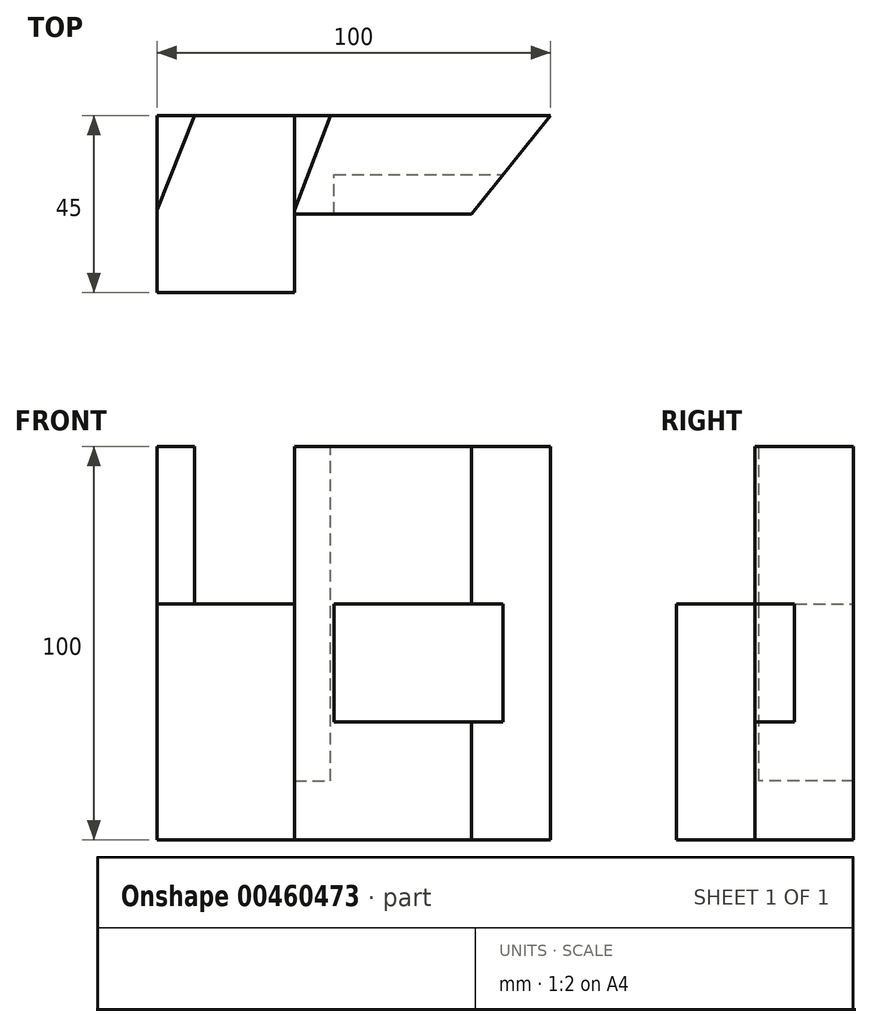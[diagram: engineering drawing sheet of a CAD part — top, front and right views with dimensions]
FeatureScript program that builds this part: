
annotation { "Feature Type Name" : "Feature", "Feature Type Description" : "" }
export const myFeature = defineFeature(function(context is Context, id is Id, definition is map)
    precondition{}
    {
        {
            var Q0;
            Q0=qCreatedBy(makeId("Top.planeOp"),FACE);
            var sketch = newSketch(context, id + "F0", { "sketchPlane" : qUnion([Q0])});
            skLineSegment(sketch, "E0.bottom", {"start": v(0, 0) * mm, "end": v(35, 0) * mm});
            skLineSegment(sketch, "E0.top", {"start": v(0, 45) * mm, "end": v(35, 45) * mm});
            skLineSegment(sketch, "E0.left", {"start": v(0, 0) * mm, "end": v(0, 45) * mm});
            skLineSegment(sketch, "E0.right", {"start": v(35, 0) * mm, "end": v(35, 45) * mm});
            skLineSegment(sketch, "E1.bottom", {"start": v(35, 45) * mm, "end": v(100, 45) * mm});
            skLineSegment(sketch, "E1.top", {"start": v(35, 20) * mm, "end": v(100, 20) * mm});
            skLineSegment(sketch, "E1.left", {"start": v(35, 45) * mm, "end": v(35, 20) * mm});
            skLineSegment(sketch, "E1.right", {"start": v(100, 45) * mm, "end": v(100, 20) * mm});
            skSolve(sketch);
        }
        {
            var Q0;
            Q0 = qSketchRegion(id + "F0", true);
            extrude(context, id + "F1", {"entities" : qUnion([Q0]), "depth" : 100 * mm});
        }
        {
            var Q0;
            Q0=makeQuery(id+"F1.opExtrude","CAP_FACE",FACE,{"disambiguationData":[OSD([sQuery(id+"F0.wireOp",EDGE,"E0.bottom"),sQuery(id+"F0.wireOp",EDGE,"E0.top"),sQuery(id+"F0.wireOp",EDGE,"E0.left"),sQuery(id+"F0.wireOp",EDGE,"E0.right"),sQuery(id+"F0.wireOp",EDGE,"E1.bottom"),sQuery(id+"F0.wireOp",EDGE,"E1.top"),sQuery(id+"F0.wireOp",EDGE,"E1.right")])],"isStart":false});
            var sketch = newSketch(context, id + "F2", { "sketchPlane" : qUnion([Q0])});
            skLineSegment(sketch, "E2", {"start": v(35, 20) * mm, "end": v(35, 21) * mm});
            skLineSegment(sketch, "E3", {"start": v(35, 21) * mm, "end": v(44.12, 45) * mm});
            skLineSegment(sketch, "E4", {"start": v(44.12, 45) * mm, "end": v(35, 45) * mm});
            skLineSegment(sketch, "E5", {"start": v(35, 45) * mm, "end": v(35, 21) * mm});
            skLineSegment(sketch, "E6", {"start": v(0, 45) * mm, "end": v(0, 21) * mm});
            skPoint(sketch, "E6.endSnap0", {"position": v(0, 22.5) * mm});
            skLineSegment(sketch, "E7", {"start": v(0, 21) * mm, "end": v(9.62, 45) * mm});
            skLineSegment(sketch, "E8", {"start": v(9.62, 45) * mm, "end": v(0, 45) * mm});
            skSolve(sketch);
        }
        {
            var Q0;
            Q0=makeQuery(id+"F1.opExtrude","CAP_FACE",FACE,{"disambiguationData":[OSD([sQuery(id+"F0.wireOp",EDGE,"E0.bottom"),sQuery(id+"F0.wireOp",EDGE,"E0.top"),sQuery(id+"F0.wireOp",EDGE,"E0.left"),sQuery(id+"F0.wireOp",EDGE,"E0.right"),sQuery(id+"F0.wireOp",EDGE,"E1.bottom"),sQuery(id+"F0.wireOp",EDGE,"E1.top"),sQuery(id+"F0.wireOp",EDGE,"E1.right")])],"isStart":true});
            cPlane(context, id + "F3", {"entities" : qUnion([Q0]), "cplaneType" : CPlaneType.OFFSET, "offset" : 60 * mm, "oppositeDirection" : true, "width" : 150 * mm, "height" : 150 * mm});
        }
        {
            var Q0;
            Q0=makeQuery(id+"F2.imprint","IMPRINT",FACE,{"disambiguationData":[TD([[makeQuery(id+"F2.imprint","IMPRINT",EDGE,{"derivedFrom":sQuery(id+"F2.wireOp",EDGE,"E2")}),1.0]])]});
            var Q1;
            Q1=qCreatedBy(id+"F3.planeOp",FACE);
            extrude(context, id + "F4", {"entities" : qUnion([Q0]), "operationType" : NewBodyOperationType.REMOVE, "endBound" : BoundingType.UP_TO_SURFACE, "oppositeDirection" : true, "endBoundEntityFace" : qUnion([Q1]), "depth" : 60 * mm});
        }
        {
            var Q0;
            Q0=makeQuery(id+"F2.imprint","IMPRINT",FACE,{"disambiguationData":[TD([[makeQuery(id+"F2.imprint","IMPRINT",EDGE,{"derivedFrom":sQuery(id+"F2.wireOp",EDGE,"E3")}),1.0]])]});
            extrude(context, id + "F5", {"entities" : qUnion([Q0]), "operationType" : NewBodyOperationType.REMOVE, "oppositeDirection" : true, "depth" : 85 * mm});
        }
        {
            var Q0;
            Q0=makeQuery(id+"F1.opExtrude","SWEPT_FACE",FACE,{"disambiguationData":[OSD([sQuery(id+"F0.wireOp",EDGE,"E1.right")])]});
            var sketch = newSketch(context, id + "F6", { "sketchPlane" : qUnion([Q0])});
            skLineSegment(sketch, "E9", {"start": v(20, 60) * mm, "end": v(20, 30) * mm});
            skLineSegment(sketch, "E10", {"start": v(20, 30) * mm, "end": v(30, 30) * mm});
            skLineSegment(sketch, "E11", {"start": v(30, 30) * mm, "end": v(30, 60) * mm});
            skLineSegment(sketch, "E12", {"start": v(30, 60) * mm, "end": v(20, 60) * mm});
            skSolve(sketch);
        }
        {
            var Q0;
            Q0 = qSketchRegion(id + "F6", true);
            extrude(context, id + "F7", {"entities" : qUnion([Q0]), "operationType" : NewBodyOperationType.REMOVE, "oppositeDirection" : true, "depth" : 55 * mm});
        }
        {
            var Q0;
            {var subQ0=sQuery(id+"F0.wireOp",EDGE,"E1.bottom");var subQ1=sQuery(id+"F0.wireOp",EDGE,"E0.top");var subQ2=sQuery(id+"F0.wireOp",EDGE,"E1.top");var subQ3=sQuery(id+"F0.wireOp",EDGE,"E1.right");var subQ4=sQuery(id+"F0.wireOp",EDGE,"E0.right");Q0=makeQuery(id+"F4.boolean.opBoolean","SPLIT",FACE,{"disambiguationData":[TD([makeQuery(id+"F1.opExtrude","SWEPT_FACE",FACE,{"disambiguationData":[OSD([subQ2])]})])],"derivedFrom":makeQuery(id+"F1.opExtrude","CAP_FACE",FACE,{"disambiguationData":[OSD([sQuery(id+"F0.wireOp",EDGE,"E0.bottom"),subQ1,sQuery(id+"F0.wireOp",EDGE,"E0.left"),subQ4,subQ0,subQ2,subQ3])],"isStart":false})});}
            var sketch = newSketch(context, id + "F8", { "sketchPlane" : qUnion([Q0])});
            skLineSegment(sketch, "E13", {"start": v(100, 45) * mm, "end": v(80, 20) * mm});
            skLineSegment(sketch, "E14", {"start": v(80, 20) * mm, "end": v(100, 20) * mm});
            skLineSegment(sketch, "E15", {"start": v(100, 20) * mm, "end": v(100, 45) * mm});
            skSolve(sketch);
        }
        {
            var Q0;
            Q0 = qSketchRegion(id + "F8", true);
            extrude(context, id + "F9", {"entities" : qUnion([Q0]), "operationType" : NewBodyOperationType.REMOVE, "endBound" : BoundingType.UP_TO_NEXT, "oppositeDirection" : true, "depth" : 25 * mm});
        }
    });
